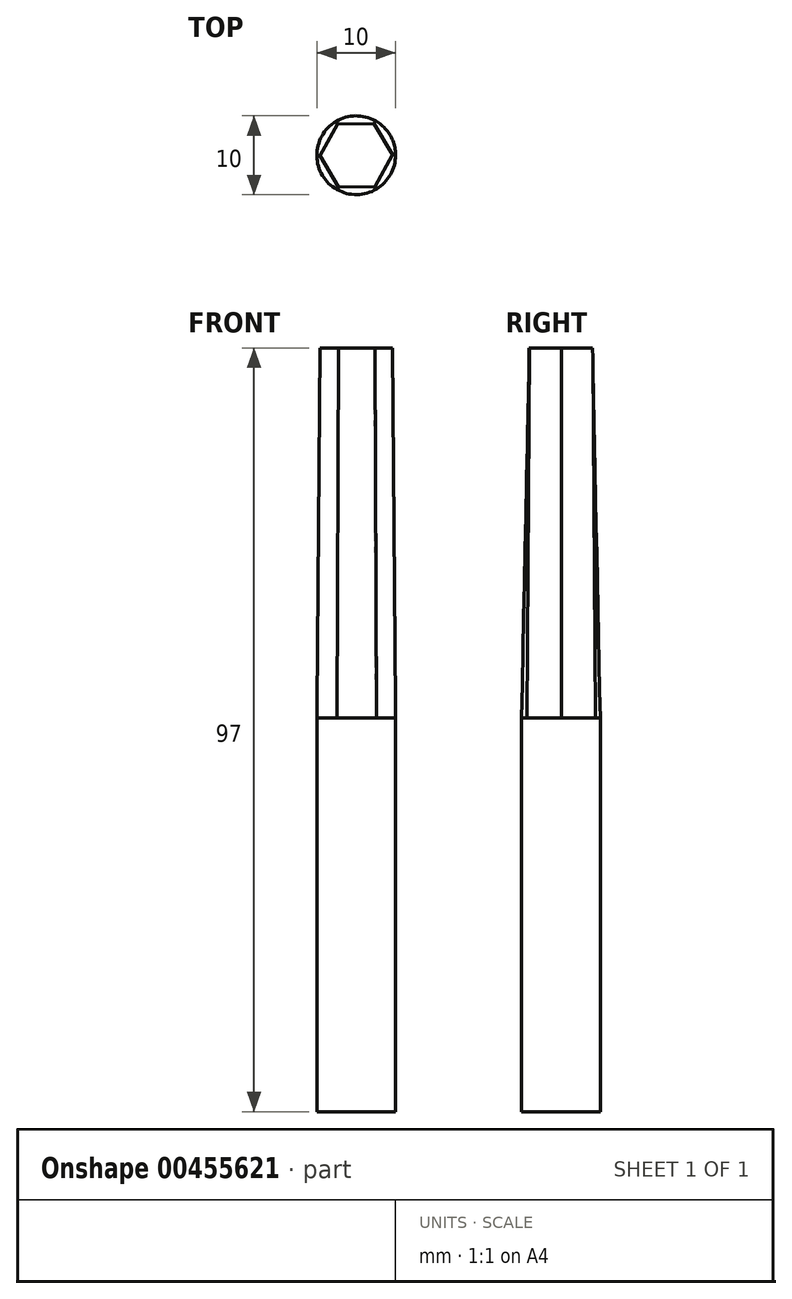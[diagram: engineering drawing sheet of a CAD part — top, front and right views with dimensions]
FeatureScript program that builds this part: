
annotation { "Feature Type Name" : "Feature", "Feature Type Description" : "" }
export const myFeature = defineFeature(function(context is Context, id is Id, definition is map)
    precondition{}
    {
        {
            var Q0;
            Q0=qCreatedBy(makeId("Top.planeOp"),FACE);
            var sketch = newSketch(context, id + "F0", { "sketchPlane" : qUnion([Q0])});
            skCircle(sketch, "E0", {"center": v(0, 0) * mm, "radius": 5 * mm});
            skSolve(sketch);
        }
        {
            var Q0;
            Q0 = qSketchRegion(id + "F0", true);
            extrude(context, id + "F1", {"entities" : qUnion([Q0]), "oppositeDirection" : true, "depth" : 50 * mm});
        }
        {
            var Q0;
            Q0=qCreatedBy(makeId("Top.planeOp"),FACE);
            cPlane(context, id + "F2", {"entities" : qUnion([Q0]), "cplaneType" : CPlaneType.OFFSET, "offset" : 47 * mm, "width" : 150 * mm, "height" : 150 * mm});
        }
        {
            var Q0;
            Q0=qCreatedBy(id+"F2.planeOp",FACE);
            var sketch = newSketch(context, id + "F3", { "sketchPlane" : qUnion([Q0])});
            skCircle(sketch, "E1.cCircle", {"center": v(0, 0) * mm, "radius": 4 * mm, "construction": true});
            skLineSegment(sketch, "E1.0", {"start": v(2.25, 4.03) * mm, "end": v(4.62, 0.07) * mm});
            skLineSegment(sketch, "E1.1", {"start": v(4.62, 0.07) * mm, "end": v(2.37, -3.96) * mm});
            skLineSegment(sketch, "E1.2", {"start": v(2.37, -3.96) * mm, "end": v(-2.25, -4.03) * mm});
            skLineSegment(sketch, "E1.3", {"start": v(-2.25, -4.03) * mm, "end": v(-4.62, -0.07) * mm});
            skLineSegment(sketch, "E1.4", {"start": v(-4.62, -0.07) * mm, "end": v(-2.37, 3.96) * mm});
            skLineSegment(sketch, "E1.5", {"start": v(-2.37, 3.96) * mm, "end": v(2.25, 4.03) * mm});
            skPoint(sketch, "E1.0.midPoint", {"position": v(3.43, 2.05) * mm});
            skSolve(sketch);
        }
        {
            var Q1;
            Q1=makeQuery(id+"F3.imprint","IMPRINT",FACE,{"disambiguationData":[TD([[makeQuery(id+"F3.imprint","IMPRINT",EDGE,{"derivedFrom":sQuery(id+"F3.wireOp",EDGE,"E1.0")}),-1.0]])]});
            var Q2;
            Q2=makeQuery(id+"F1.opExtrude","CAP_FACE",FACE,{"disambiguationData":[OSD([sQuery(id+"F0.wireOp",EDGE,"E0")])],"isStart":true});
            loft(context, id + "F4", {"operationType" : NewBodyOperationType.ADD, "sheetProfilesArray" : [{ "sheetProfileEntities" : qUnion([Q1]) }, { "sheetProfileEntities" : qUnion([Q2]) }]});
        }
    });
